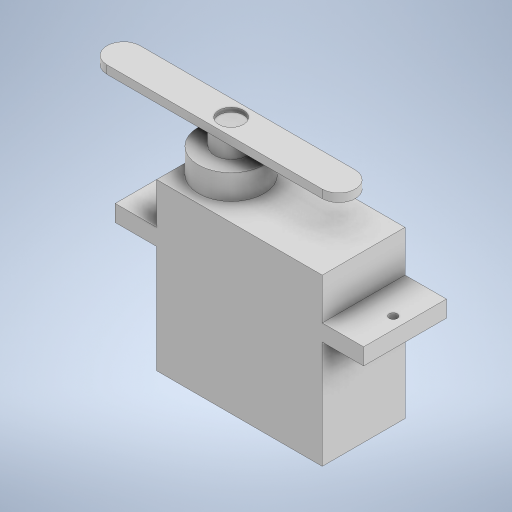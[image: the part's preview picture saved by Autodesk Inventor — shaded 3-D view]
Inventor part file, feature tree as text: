
AUTODESK INVENTOR PART (.ipt)
format: ipt  version: 2023 (Build 270158000, 158)  size: 291,328 bytes
history: native  units: in
note: dims shown in document units (in); Inventor stores cm internally (conversion verified against a paired STEP export)
features: extrude x8, sketch x8
ambient origin geometry x8: Origin, YZ Plane, XZ Plane, XY Plane, X Axis, Y Axis, Z Axis, Center Point
bodies: Solid1 (feature_tree)
feature tree (16):
  extrude  "Extrusion1"  Depth=0.7874in
  extrude  "Extrusion2"  Depth=0.3937in
  extrude  "Extrusion3"  Depth=0.1969in TaperAngle=0.0deg
  extrude  "Extrusion4"  Depth=0.1969in TaperAngle=0.0deg
  extrude  "Extrusion5"  TaperAngle=0.0deg  [1 undecoded]
  extrude  "Extrusion6"  Depth=0.1575in
  extrude  "Extrusion7"  Depth=0.5906in
  extrude  "Extrusion8"  Depth=0.0787in
  sketch  "Sketch1"  dims[d0=0.7874in d1=0.7874in]
  sketch  "Sketch2"  dims[d2=0.3937in d3=0.0in d4=0.3937in]
  sketch  "Sketch3"  dims[d5=0.0787in d6=0.1969in d7=0.0in]
  sketch  "Sketch4"  dims[d8=0.0787in d9=0.1969in d10=0.0in]
  sketch  "Sketch5"  dims[d11=0.0394in d12=0.0in d13=0.0in]
  sketch  "Sketch6"  dims[d14=0.1181in d15=0.0in d16=0.1575in]
  sketch  "Sketch7"  dims[d17=0.0787in d18=0.0in d19=0.5906in]
  sketch  "Sketch8"  dims[d20=0.5906in d21=0.0787in d22=0.0394in d23=0.0in d24=0.1181in d25=0.0197in d26=0.0in]
note: 1 required parameter value undecoded (feature->parameter linkage not recoverable at this tier; creation-order binding heuristic only, values carry confidence <= 0.55)
